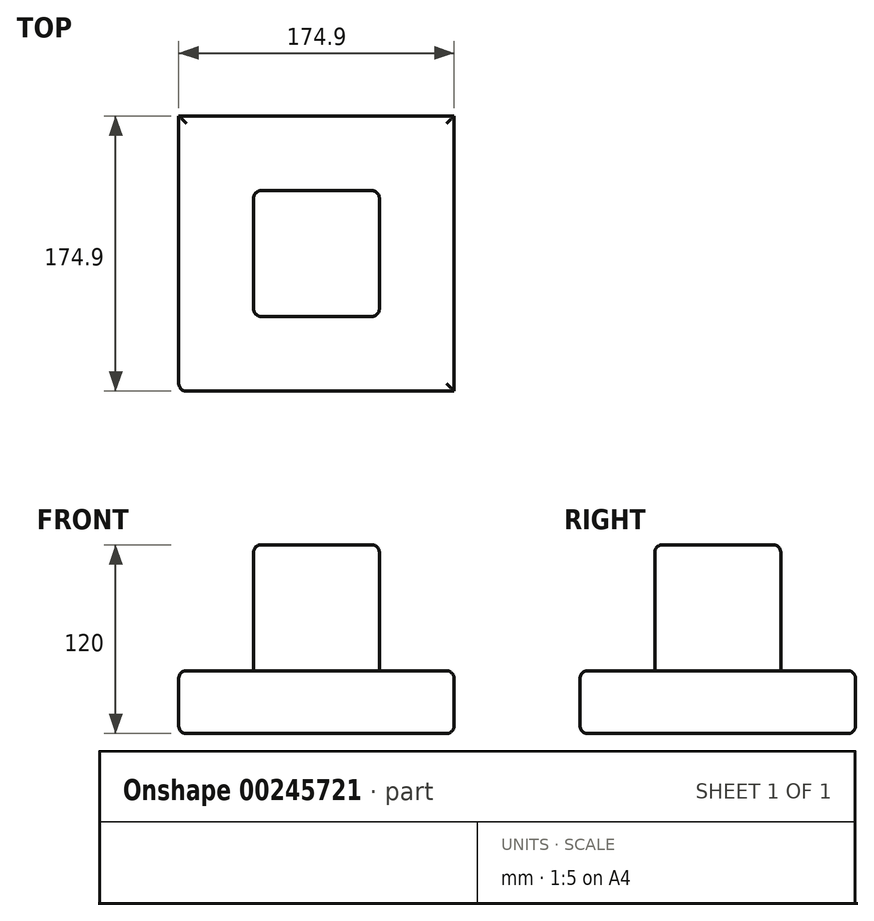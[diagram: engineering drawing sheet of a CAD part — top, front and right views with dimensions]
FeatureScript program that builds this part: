
annotation { "Feature Type Name" : "Feature", "Feature Type Description" : "" }
export const myFeature = defineFeature(function(context is Context, id is Id, definition is map)
    precondition{}
    {
        {
            var Q0;
            Q0=qCreatedBy(makeId("Top.planeOp"),FACE);
            var sketch = newSketch(context, id + "F0", { "sketchPlane" : qUnion([Q0])});
            skLineSegment(sketch, "E0", {"start": v(87.45, 87.45) * mm, "end": v(87.45, -87.45) * mm});
            skLineSegment(sketch, "E1", {"start": v(-87.45, 87.45) * mm, "end": v(-87.45, -87.45) * mm});
            skLineSegment(sketch, "E2", {"start": v(87.45, 87.45) * mm, "end": v(-87.45, 87.45) * mm});
            skLineSegment(sketch, "E3", {"start": v(87.45, -87.45) * mm, "end": v(-87.45, -87.45) * mm});
            skLineSegment(sketch, "E4", {"start": v(0, -40) * mm, "end": v(40, -40) * mm});
            skLineSegment(sketch, "E5", {"start": v(0, -40) * mm, "end": v(-40, -40) * mm});
            skLineSegment(sketch, "E6", {"start": v(40, -40) * mm, "end": v(40, 40) * mm});
            skLineSegment(sketch, "E7", {"start": v(40, 40) * mm, "end": v(-40, 40) * mm});
            skLineSegment(sketch, "E8", {"start": v(-40, 40) * mm, "end": v(-40, -40) * mm});
            skSolve(sketch);
        }
        {
            var Q0;
            Q0=makeQuery(id+"F0.imprint","IMPRINT",FACE,{"disambiguationData":[TD([[makeQuery(id+"F0.imprint","IMPRINT",EDGE,{"derivedFrom":sQuery(id+"F0.wireOp",EDGE,"E0")}),-1.0]])]});
            extrude(context, id + "F1", {"entities" : qUnion([Q0]), "depth" : 40 * mm});
        }
        {
            var Q0;
            Q0=makeQuery(id+"F0.imprint","IMPRINT",FACE,{"disambiguationData":[TD([[makeQuery(id+"F0.imprint","IMPRINT",EDGE,{"derivedFrom":sQuery(id+"F0.wireOp",EDGE,"E4")}),1.0]])]});
            extrude(context, id + "F2", {"entities" : qUnion([Q0]), "operationType" : NewBodyOperationType.ADD, "depth" : 120 * mm});
        }
        {
            var Q0;
            Q0=makeQuery(id+"F2.opExtrude","CAP_EDGE",EDGE,{"disambiguationData":[OSD([sQuery(id+"F0.wireOp",EDGE,"E4"),sQuery(id+"F0.wireOp",EDGE,"E5")])],"isStart":false});
            var Q1;
            Q1=makeQuery(id+"F2.opExtrude","CAP_EDGE",EDGE,{"disambiguationData":[OSD([sQuery(id+"F0.wireOp",EDGE,"E6")])],"isStart":false});
            var Q2;
            Q2=makeQuery(id+"F2.opExtrude","CAP_EDGE",EDGE,{"disambiguationData":[OSD([sQuery(id+"F0.wireOp",EDGE,"E8")])],"isStart":false});
            var Q3;
            Q3=makeQuery(id+"F2.opExtrude","CAP_EDGE",EDGE,{"disambiguationData":[OSD([sQuery(id+"F0.wireOp",EDGE,"E7")])],"isStart":false});
            var Q4;
            Q4=makeQuery(id+"F2.opExtrude","SWEPT_EDGE",EDGE,{"disambiguationData":[OSD([sQuery(id+"F0.wireOp",EDGE,"E6"),sQuery(id+"F0.wireOp",EDGE,"E7")])]});
            var Q5;
            Q5=makeQuery(id+"F2.opExtrude","SWEPT_EDGE",EDGE,{"disambiguationData":[OSD([sQuery(id+"F0.wireOp",EDGE,"E4"),sQuery(id+"F0.wireOp",EDGE,"E6")])]});
            var Q6;
            Q6=makeQuery(id+"F2.opExtrude","SWEPT_EDGE",EDGE,{"disambiguationData":[OSD([sQuery(id+"F0.wireOp",EDGE,"E5"),sQuery(id+"F0.wireOp",EDGE,"E8")])]});
            var Q7;
            Q7=makeQuery(id+"F2.opExtrude","SWEPT_EDGE",EDGE,{"disambiguationData":[OSD([sQuery(id+"F0.wireOp",EDGE,"E7"),sQuery(id+"F0.wireOp",EDGE,"E8")])]});
            var Q8;
            Q8=makeQuery(id+"F1.opExtrude","CAP_EDGE",EDGE,{"disambiguationData":[OSD([sQuery(id+"F0.wireOp",EDGE,"E1")])],"isStart":false});
            var Q9;
            Q9=makeQuery(id+"F1.opExtrude","CAP_EDGE",EDGE,{"disambiguationData":[OSD([sQuery(id+"F0.wireOp",EDGE,"E3")])],"isStart":false});
            var Q10;
            Q10=makeQuery(id+"F1.opExtrude","CAP_EDGE",EDGE,{"disambiguationData":[OSD([sQuery(id+"F0.wireOp",EDGE,"E3")])],"isStart":true});
            var Q11;
            Q11=makeQuery(id+"F1.opExtrude","CAP_EDGE",EDGE,{"disambiguationData":[OSD([sQuery(id+"F0.wireOp",EDGE,"E1")])],"isStart":true});
            var Q12;
            Q12=makeQuery(id+"F1.opExtrude","SWEPT_EDGE",EDGE,{"disambiguationData":[OSD([sQuery(id+"F0.wireOp",EDGE,"E1"),sQuery(id+"F0.wireOp",EDGE,"E3")])]});
            var Q13;
            Q13=makeQuery(id+"F1.opExtrude","CAP_EDGE",EDGE,{"disambiguationData":[OSD([sQuery(id+"F0.wireOp",EDGE,"E0")])],"isStart":false});
            var Q14;
            Q14=makeQuery(id+"F1.opExtrude","CAP_EDGE",EDGE,{"disambiguationData":[OSD([sQuery(id+"F0.wireOp",EDGE,"E0")])],"isStart":true});
            var Q15;
            Q15=makeQuery(id+"F1.opExtrude","CAP_EDGE",EDGE,{"disambiguationData":[OSD([sQuery(id+"F0.wireOp",EDGE,"E2")])],"isStart":true});
            var Q16;
            Q16=makeQuery(id+"F1.opExtrude","CAP_EDGE",EDGE,{"disambiguationData":[OSD([sQuery(id+"F0.wireOp",EDGE,"E2")])],"isStart":false});
            fillet(context, id + "F3", {"entities" : qUnion([Q0, Q1, Q2, Q3, Q4, Q5, Q6, Q7, Q8, Q9, Q10, Q11, Q12, Q13, Q14, Q15, Q16]), "radius" : 5 * mm, "tangentPropagation" : true, "allowEdgeOverflow" : false});
        }
    });
